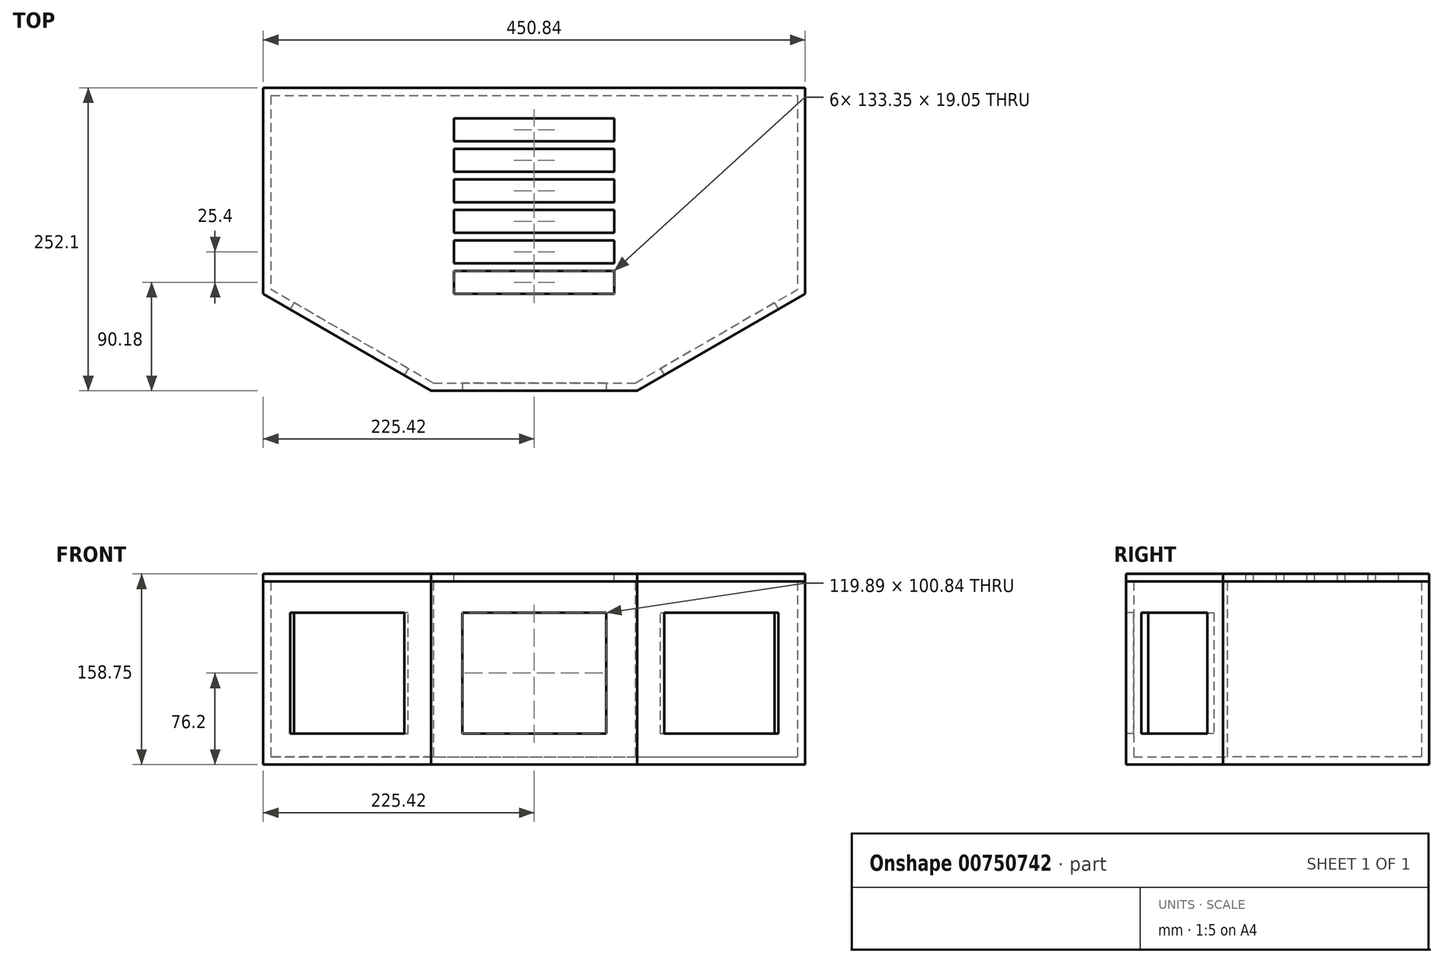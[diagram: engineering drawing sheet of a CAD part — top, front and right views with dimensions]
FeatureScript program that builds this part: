
annotation { "Feature Type Name" : "Feature", "Feature Type Description" : "" }
export const myFeature = defineFeature(function(context is Context, id is Id, definition is map)
    precondition{}
    {
        {
            var Q0;
            Q0=qCreatedBy(makeId("Top.planeOp"),FACE);
            var sketch = newSketch(context, id + "F0", { "sketchPlane" : qUnion([Q0])});
            skLineSegment(sketch, "E0.bottom", {"start": v(85.73, 85.73) * mm, "end": v(-85.73, 85.73) * mm, "construction": true});
            skLineSegment(sketch, "E0.top", {"start": v(85.73, -85.72) * mm, "end": v(-85.73, -85.72) * mm, "construction": true});
            skLineSegment(sketch, "E0.left", {"start": v(85.73, 85.73) * mm, "end": v(85.73, -85.72) * mm, "construction": true});
            skLineSegment(sketch, "E0.right", {"start": v(-85.73, 85.73) * mm, "end": v(-85.73, -85.72) * mm, "construction": true});
            skPoint(sketch, "E0.middle", {"position": v(0, 0) * mm});
            skLineSegment(sketch, "E1", {"start": v(85.73, 85.73) * mm, "end": v(98.43, 85.73) * mm, "construction": true});
            skLineSegment(sketch, "E2", {"start": v(98.43, 85.73) * mm, "end": v(225.43, 85.73) * mm, "construction": true});
            skLineSegment(sketch, "E3", {"start": v(-85.73, 85.73) * mm, "end": v(-225.43, 85.73) * mm, "construction": true});
            skLineSegment(sketch, "E4.bottom", {"start": v(-225.43, 85.73) * mm, "end": v(225.43, 85.73) * mm});
            skLineSegment(sketch, "E4.top", {"start": v(-85.72, -166.38) * mm, "end": v(85.73, -166.38) * mm});
            skLineSegment(sketch, "E4.left", {"start": v(-225.43, 85.72) * mm, "end": v(-225.43, -85.72) * mm});
            skLineSegment(sketch, "E4.right", {"start": v(225.43, 85.72) * mm, "end": v(225.43, -85.72) * mm});
            skLineSegment(sketch, "E5", {"start": v(-85.72, -166.38) * mm, "end": v(-225.43, -85.72) * mm});
            skLineSegment(sketch, "E6", {"start": v(85.73, -166.38) * mm, "end": v(225.43, -85.72) * mm});
            skLineSegment(sketch, "E7", {"start": v(0, -166.38) * mm, "end": v(0, -191.5) * mm, "construction": true});
            skLineSegment(sketch, "E8", {"start": v(0, -191.5) * mm, "end": v(59.94, -191.5) * mm, "construction": true});
            skLineSegment(sketch, "E9.MirrorCS", {"start": v(0, -191.5) * mm, "end": v(-59.94, -191.5) * mm, "construction": true});
            skSolve(sketch);
        }
        {
            var Q0;
            Q0 = qSketchRegion(id + "F0", true);
            extrude(context, id + "F1", {"entities" : qUnion([Q0]), "depth" : 152.4 * mm, "offsetDistance" : 25.4 * mm});
        }
        {
            var Q0;
            Q0=makeQuery(id+"F1.opExtrude","SWEPT_FACE",FACE,{"disambiguationData":[OSD([sQuery(id+"F0.wireOp",EDGE,"E4.top")])]});
            var sketch = newSketch(context, id + "F2", { "sketchPlane" : qUnion([Q0])});
            skPoint(sketch, "E10.0", {"position": v(-59.94, 0) * mm});
            skPoint(sketch, "E11.0", {"position": v(59.94, 0) * mm});
            skLineSegment(sketch, "E12.0", {"start": v(-59.94, 25.78) * mm, "end": v(59.94, 25.78) * mm});
            skLineSegment(sketch, "E12.1", {"start": v(-59.94, 126.62) * mm, "end": v(-59.94, 25.78) * mm});
            skLineSegment(sketch, "E12.2", {"start": v(59.94, 126.62) * mm, "end": v(-59.94, 126.62) * mm});
            skLineSegment(sketch, "E12.3", {"start": v(59.94, 25.78) * mm, "end": v(59.94, 126.62) * mm});
            skSolve(sketch);
        }
        {
            var Q0;
            Q0=makeQuery(id+"F1.opExtrude","CAP_FACE",FACE,{"disambiguationData":[OSD([sQuery(id+"F0.wireOp",EDGE,"E4.bottom"),sQuery(id+"F0.wireOp",EDGE,"E4.top"),sQuery(id+"F0.wireOp",EDGE,"E4.left"),sQuery(id+"F0.wireOp",EDGE,"E4.right"),sQuery(id+"F0.wireOp",EDGE,"E5"),sQuery(id+"F0.wireOp",EDGE,"E6")])],"isStart":false});
            shell(context, id + "F3", {"entities" : qUnion([Q0]), "thickness" : 6.35 * mm});
        }
        {
            var Q0;
            Q0 = qSketchRegion(id + "F2", true);
            extrude(context, id + "F4", {"entities" : qUnion([Q0]), "operationType" : NewBodyOperationType.REMOVE, "oppositeDirection" : true, "depth" : 25.4 * mm, "offsetDistance" : 25.4 * mm});
        }
        {
            var Q0;
            Q0=makeQuery(id+"F1.opExtrude","CAP_FACE",FACE,{"disambiguationData":[OSD([sQuery(id+"F0.wireOp",EDGE,"E4.bottom"),sQuery(id+"F0.wireOp",EDGE,"E4.top"),sQuery(id+"F0.wireOp",EDGE,"E4.left"),sQuery(id+"F0.wireOp",EDGE,"E4.right"),sQuery(id+"F0.wireOp",EDGE,"E5"),sQuery(id+"F0.wireOp",EDGE,"E6")])],"isStart":false});
            var sketch = newSketch(context, id + "F5", { "sketchPlane" : qUnion([Q0])});
            skLineSegment(sketch, "E13.0", {"start": v(-85.72, -166.38) * mm, "end": v(-225.43, -85.72) * mm});
            skLineSegment(sketch, "E14.0", {"start": v(-225.43, 85.72) * mm, "end": v(-225.43, -85.72) * mm});
            skLineSegment(sketch, "E15.0", {"start": v(-225.43, 85.73) * mm, "end": v(225.43, 85.73) * mm});
            skLineSegment(sketch, "E16.0", {"start": v(225.43, 85.72) * mm, "end": v(225.43, -85.72) * mm});
            skLineSegment(sketch, "E17.0", {"start": v(85.73, -166.38) * mm, "end": v(225.43, -85.72) * mm});
            skLineSegment(sketch, "E18.0", {"start": v(-85.72, -166.38) * mm, "end": v(85.73, -166.38) * mm});
            skSolve(sketch);
        }
        {
            var Q0;
            Q0 = qSketchRegion(id + "F5", true);
            extrude(context, id + "F6", {"entities" : qUnion([Q0]), "depth" : 6.35 * mm, "offsetDistance" : 25.4 * mm});
        }
        {
            var Q0;
            Q0=makeQuery(id+"F6.opExtrude","CAP_FACE",FACE,{"disambiguationData":[OSD([sQuery(id+"F5.wireOp",EDGE,"E13.0"),sQuery(id+"F5.wireOp",EDGE,"E14.0"),sQuery(id+"F5.wireOp",EDGE,"E15.0"),sQuery(id+"F5.wireOp",EDGE,"E16.0"),sQuery(id+"F5.wireOp",EDGE,"E17.0"),sQuery(id+"F5.wireOp",EDGE,"E18.0")])],"isStart":false});
            var sketch = newSketch(context, id + "F7", { "sketchPlane" : qUnion([Q0])});
            skLineSegment(sketch, "E19.bottom", {"start": v(66.68, 9.53) * mm, "end": v(-66.68, 9.53) * mm});
            skLineSegment(sketch, "E19.top", {"start": v(66.68, -9.53) * mm, "end": v(-66.68, -9.53) * mm});
            skLineSegment(sketch, "E19.left", {"start": v(66.68, 9.53) * mm, "end": v(66.68, -9.53) * mm});
            skLineSegment(sketch, "E19.right", {"start": v(-66.68, 9.53) * mm, "end": v(-66.68, -9.53) * mm});
            skPoint(sketch, "E19.middle", {"position": v(0, 0) * mm});
            skLineSegment(sketch, "E20.0.1.0", {"start": v(66.68, -15.87) * mm, "end": v(-66.68, -15.87) * mm});
            skLineSegment(sketch, "E20.0.1.1", {"start": v(66.68, -15.87) * mm, "end": v(66.68, -34.92) * mm});
            skLineSegment(sketch, "E20.0.1.2", {"start": v(66.68, -34.92) * mm, "end": v(-66.68, -34.92) * mm});
            skLineSegment(sketch, "E20.0.1.3", {"start": v(-66.68, -15.87) * mm, "end": v(-66.68, -34.92) * mm});
            skLineSegment(sketch, "E20.0.2.0", {"start": v(66.68, -41.27) * mm, "end": v(-66.68, -41.27) * mm});
            skLineSegment(sketch, "E20.0.2.1", {"start": v(66.68, -41.27) * mm, "end": v(66.68, -60.32) * mm});
            skLineSegment(sketch, "E20.0.2.2", {"start": v(66.68, -60.32) * mm, "end": v(-66.68, -60.32) * mm});
            skLineSegment(sketch, "E20.0.2.3", {"start": v(-66.68, -41.27) * mm, "end": v(-66.68, -60.32) * mm});
            skLineSegment(sketch, "E20.direction1", {"start": v(-66.68, 9.53) * mm, "end": v(-48.51, 3.81) * mm, "construction": true});
            skLineSegment(sketch, "E20.direction2", {"start": v(-66.68, 9.53) * mm, "end": v(-66.68, -15.87) * mm, "construction": true});
            skLineSegment(sketch, "E21.0.1.0", {"start": v(66.68, 34.93) * mm, "end": v(-66.68, 34.93) * mm});
            skLineSegment(sketch, "E21.0.1.1", {"start": v(66.68, 34.93) * mm, "end": v(66.68, 15.87) * mm});
            skLineSegment(sketch, "E21.0.1.2", {"start": v(66.68, 15.87) * mm, "end": v(-66.68, 15.87) * mm});
            skLineSegment(sketch, "E21.0.2.0", {"start": v(66.68, 60.33) * mm, "end": v(-66.68, 60.33) * mm});
            skLineSegment(sketch, "E21.0.2.1", {"start": v(66.68, 60.33) * mm, "end": v(66.68, 41.27) * mm});
            skLineSegment(sketch, "E21.0.2.2", {"start": v(66.68, 41.27) * mm, "end": v(-66.68, 41.27) * mm});
            skLineSegment(sketch, "E21.direction1", {"start": v(-66.68, 9.53) * mm, "end": v(-28.58, 9.53) * mm, "construction": true});
            skLineSegment(sketch, "E21.direction2", {"start": v(-66.68, 9.53) * mm, "end": v(-66.68, 34.93) * mm, "construction": true});
            skLineSegment(sketch, "E22.0.0.3", {"start": v(66.68, -66.68) * mm, "end": v(-66.67, -66.68) * mm});
            skLineSegment(sketch, "E22.3.0.3", {"start": v(66.68, -66.68) * mm, "end": v(66.68, -85.73) * mm});
            skLineSegment(sketch, "E22.6.0.3", {"start": v(66.68, -85.73) * mm, "end": v(-66.67, -85.73) * mm});
            skLineSegment(sketch, "E22.9.0.3", {"start": v(-66.67, -66.68) * mm, "end": v(-66.67, -85.73) * mm});
            skLineSegment(sketch, "E23", {"start": v(-66.68, 60.33) * mm, "end": v(-66.68, 41.27) * mm});
            skLineSegment(sketch, "E24", {"start": v(-66.68, 34.93) * mm, "end": v(-66.68, 15.87) * mm});
            skSolve(sketch);
        }
        {
            var Q0;
            Q0 = qSketchRegion(id + "F7", true);
            extrude(context, id + "F8", {"entities" : qUnion([Q0]), "operationType" : NewBodyOperationType.REMOVE, "oppositeDirection" : true, "depth" : 25.4 * mm, "offsetDistance" : 25.4 * mm});
        }
        {
            var Q0;
            Q0=makeQuery(id+"F1.opExtrude","SWEPT_FACE",FACE,{"disambiguationData":[OSD([sQuery(id+"F0.wireOp",EDGE,"E6")])]});
            var sketch = newSketch(context, id + "F9", { "sketchPlane" : qUnion([Q0])});
            skLineSegment(sketch, "E25.0", {"start": v(16.83, 25.78) * mm, "end": v(126.58, 25.78) * mm});
            skLineSegment(sketch, "E25.1", {"start": v(16.83, 126.62) * mm, "end": v(16.83, 25.78) * mm});
            skLineSegment(sketch, "E25.2", {"start": v(126.58, 126.62) * mm, "end": v(16.83, 126.62) * mm});
            skLineSegment(sketch, "E25.3", {"start": v(126.58, 25.78) * mm, "end": v(126.58, 126.62) * mm});
            skSolve(sketch);
        }
        {
            var Q0;
            Q0 = qSketchRegion(id + "F9", true);
            extrude(context, id + "F10", {"entities" : qUnion([Q0]), "operationType" : NewBodyOperationType.REMOVE, "oppositeDirection" : true, "depth" : 25.4 * mm, "offsetDistance" : 25.4 * mm});
        }
        {
            var Q0;
            Q0=makeQuery(id+"F1.opExtrude","SWEPT_FACE",FACE,{"disambiguationData":[OSD([sQuery(id+"F0.wireOp",EDGE,"E5")])]});
            var sketch = newSketch(context, id + "F11", { "sketchPlane" : qUnion([Q0])});
            skLineSegment(sketch, "E26.0", {"start": v(-126.58, 25.78) * mm, "end": v(-16.83, 25.78) * mm});
            skLineSegment(sketch, "E26.1", {"start": v(-126.58, 126.62) * mm, "end": v(-126.58, 25.78) * mm});
            skLineSegment(sketch, "E26.2", {"start": v(-16.83, 126.62) * mm, "end": v(-126.58, 126.62) * mm});
            skLineSegment(sketch, "E26.3", {"start": v(-16.83, 25.78) * mm, "end": v(-16.83, 126.62) * mm});
            skSolve(sketch);
        }
        {
            var Q0;
            Q0 = qSketchRegion(id + "F11", true);
            extrude(context, id + "F12", {"entities" : qUnion([Q0]), "operationType" : NewBodyOperationType.REMOVE, "oppositeDirection" : true, "depth" : 25.4 * mm, "offsetDistance" : 25.4 * mm});
        }
    });
